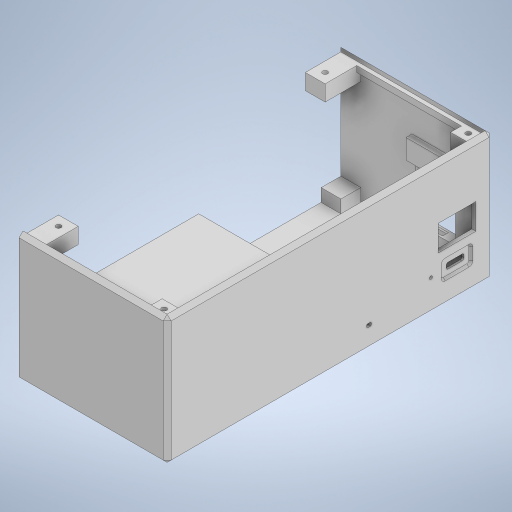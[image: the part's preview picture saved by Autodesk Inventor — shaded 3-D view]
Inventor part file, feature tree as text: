
AUTODESK INVENTOR PART (.ipt)
format: ipt  version: 2024.2 (Build 282272000, 272)  size: 573,440 bytes
history: native  units: in
note: dims shown in document units (in); Inventor stores cm internally (conversion verified against a paired STEP export)
features: extrude x25, sketch x13, chamfer x4, projected_geometry x2
ambient origin geometry x8: Origin, YZ Plane, XZ Plane, XY Plane, X Axis, Y Axis, Z Axis, Center Point
bodies: Solide1 (feature_tree)
feature tree (44):
  sketch  "Esquisse1"
  extrude  "Extrusion1"  Depth=2.9528in
  extrude  "Extrusion2"  Depth=2.5591in
  extrude  "Extrusion5"  Depth=1.2795in
  extrude  "Extrusion7"  Depth=0.0787in
  sketch  "Esquisse8"
  extrude  "Extrusion8"  Depth=0.0787in
  extrude  "Extrusion9"  Depth=0.0787in TaperAngle=0.0deg
  extrude  "Extrusion10"  Depth=6.3386in TaperAngle=0.0deg
  extrude  "Extrusion11"  Depth=0.0787in TaperAngle=0.0deg
  extrude  "Extrusion12"  Depth=0.0787in
  sketch  "Esquisse9"
  extrude  "Extrusion13"  Depth=0.1378in
  extrude  "Extrusion14"  Depth=0.3346in
  extrude  "Extrusion15"  Depth=0.0787in
  chamfer  "Chanfrein1"  Distance=0.1772in
  extrude  "Extrusion16"  Depth=0.374in
  extrude  "Extrusion18"  Depth=0.3937in
  sketch  "Esquisse12"
  extrude  "Extrusion19"  Depth=0.5906in
  extrude  "Extrusion20"  Depth=0.5906in
  extrude  "Extrusion17"  Depth=0.3937in
  sketch  "Esquisse13"
  extrude  "Extrusion21"  Depth=0.2559in TaperAngle=0.0deg
  extrude  "Extrusion22"  Depth=0.2441in
  chamfer  "Chanfrein2"  Distance=0.1181in
  extrude  "Extrusion23"  Depth=0.315in
  extrude  "Extrusion24"  Depth=0.5512in
  extrude  "Extrusion25"  Depth=0.3543in
  extrude  "Extrusion26"  Depth=0.0984in
  extrude  "Extrusion27"  Depth=0.4606in
  extrude  "Extrusion28"  Depth=0.0394in
  chamfer  "Chanfrein3"  Distance=0.3937in
  chamfer  "Chanfrein4"  Distance=0.0394in
  sketch  "Esquisse4"
  sketch  "Esquisse7"
  sketch  "Esquisse10"
  sketch  "Esquisse11"
  sketch  "Esquisse14"
  sketch  "Esquisse16"
  sketch  "Esquisse17"
  sketch  "Esquisse18"
  projected_geometry  "Boucle projetée1"
  projected_geometry  "Boucle projetée2"
